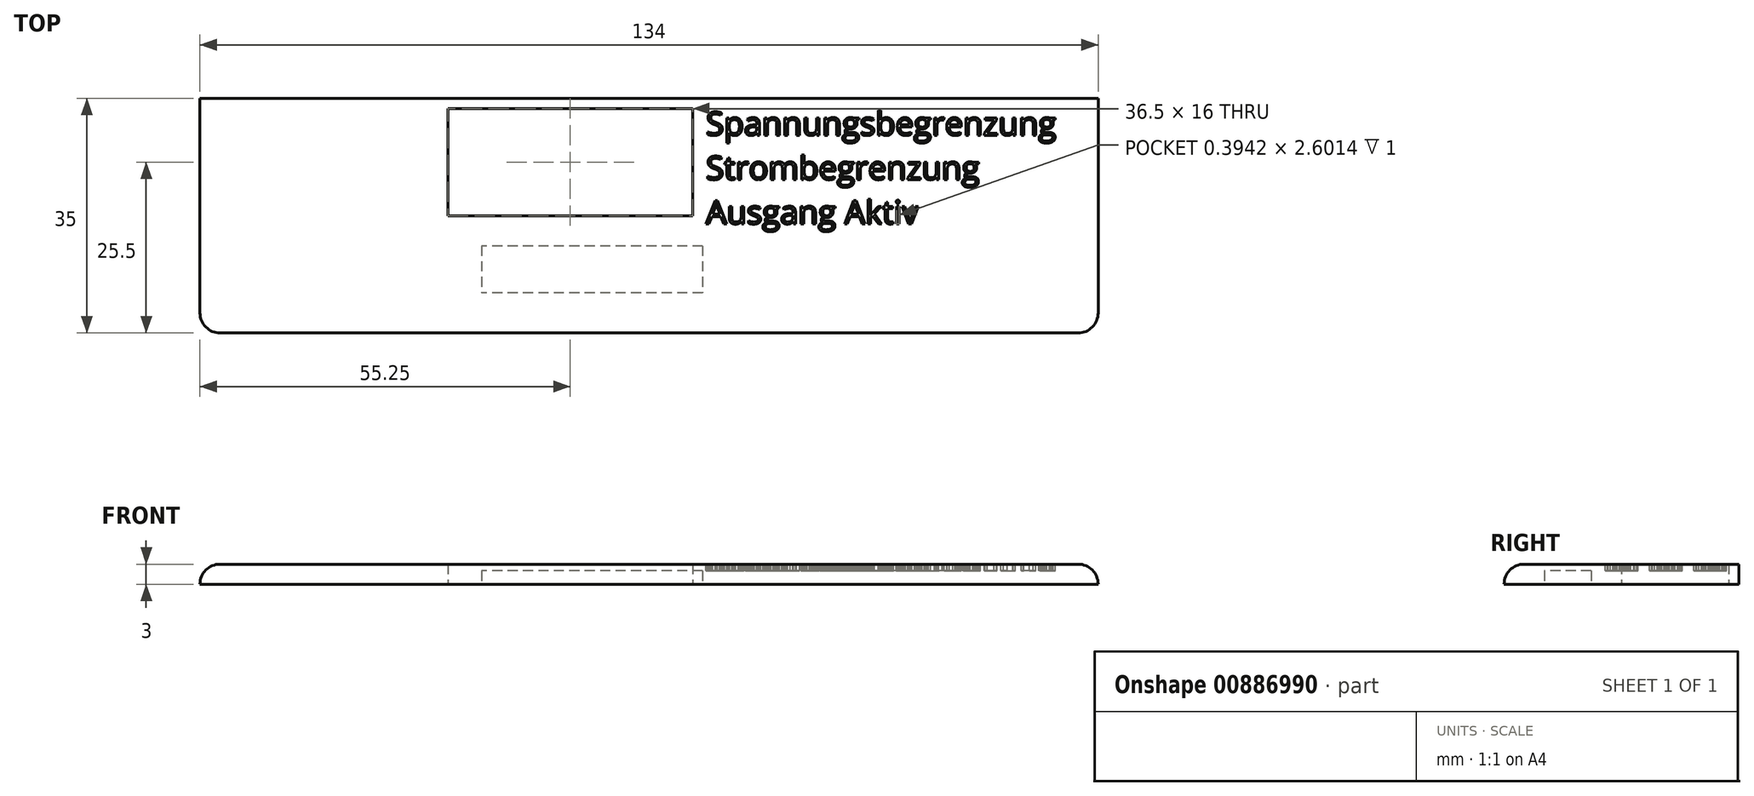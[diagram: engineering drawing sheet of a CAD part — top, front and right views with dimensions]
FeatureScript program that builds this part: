
annotation { "Feature Type Name" : "Feature", "Feature Type Description" : "" }
export const myFeature = defineFeature(function(context is Context, id is Id, definition is map)
    precondition{}
    {
        {
            var Q0;
            Q0=qCreatedBy(makeId("Top.planeOp"),FACE);
            var sketch = newSketch(context, id + "F0", { "sketchPlane" : qUnion([Q0])});
            skLineSegment(sketch, "E0.bottom", {"start": v(0, 0) * mm, "end": v(-134, 0) * mm});
            skLineSegment(sketch, "E0.top", {"start": v(0, -35) * mm, "end": v(-134, -35) * mm});
            skLineSegment(sketch, "E0.left", {"start": v(0, 0) * mm, "end": v(0, -35) * mm});
            skLineSegment(sketch, "E0.right", {"start": v(-134, 0) * mm, "end": v(-134, -35) * mm});
            skLineSegment(sketch, "E1.bottom", {"start": v(-97, -1.5) * mm, "end": v(-60.5, -1.5) * mm});
            skLineSegment(sketch, "E1.top", {"start": v(-97, -17.5) * mm, "end": v(-60.5, -17.5) * mm});
            skLineSegment(sketch, "E1.left", {"start": v(-97, -1.5) * mm, "end": v(-97, -17.5) * mm});
            skLineSegment(sketch, "E1.right", {"start": v(-60.5, -1.5) * mm, "end": v(-60.5, -17.5) * mm});
            skLineSegment(sketch, "E2.bottom", {"start": v(-59, -22) * mm, "end": v(-92, -22) * mm});
            skLineSegment(sketch, "E2.top", {"start": v(-59, -29) * mm, "end": v(-92, -29) * mm});
            skLineSegment(sketch, "E2.left", {"start": v(-59, -22) * mm, "end": v(-59, -29) * mm});
            skLineSegment(sketch, "E2.right", {"start": v(-92, -22) * mm, "end": v(-92, -29) * mm});
            skSolve(sketch);
        }
        {
            var Q0;
            Q0=makeQuery(id+"F0.imprint","IMPRINT",FACE,{"disambiguationData":[TD([[makeQuery(id+"F0.imprint","IMPRINT",EDGE,{"derivedFrom":sQuery(id+"F0.wireOp",EDGE,"E0.bottom")}),1.0]])]});
            var Q1;
            Q1=makeQuery(id+"F0.imprint","IMPRINT",FACE,{"disambiguationData":[TD([[makeQuery(id+"F0.imprint","IMPRINT",EDGE,{"derivedFrom":sQuery(id+"F0.wireOp",EDGE,"E2.bottom")}),1.0]])]});
            extrude(context, id + "F1", {"entities" : qUnion([Q0, Q1]), "depth" : 3 * mm, "offsetDistance" : 25 * mm});
        }
        {
            var Q0;
            Q0=makeQuery(id+"F1.opExtrude","CAP_EDGE",EDGE,{"disambiguationData":[OSD([sQuery(id+"F0.wireOp",EDGE,"E0.top")])],"isStart":false});
            var Q1;
            Q1=makeQuery(id+"F1.opExtrude","CAP_EDGE",EDGE,{"disambiguationData":[OSD([sQuery(id+"F0.wireOp",EDGE,"E0.right")])],"isStart":false});
            var Q2;
            Q2=makeQuery(id+"F1.opExtrude","CAP_EDGE",EDGE,{"disambiguationData":[OSD([sQuery(id+"F0.wireOp",EDGE,"E0.left")])],"isStart":false});
            var Q3;
            Q3=makeQuery(id+"F1.opExtrude","SWEPT_EDGE",EDGE,{"disambiguationData":[OSD([sQuery(id+"F0.wireOp",EDGE,"E0.top"),sQuery(id+"F0.wireOp",EDGE,"E0.right")])]});
            var Q4;
            Q4=makeQuery(id+"F1.opExtrude","SWEPT_EDGE",EDGE,{"disambiguationData":[OSD([sQuery(id+"F0.wireOp",EDGE,"E0.top"),sQuery(id+"F0.wireOp",EDGE,"E0.left")])]});
            fillet(context, id + "F2", {"entities" : qUnion([Q0, Q1, Q2, Q3, Q4]), "radius" : 3 * mm, "tangentPropagation" : true, "allowEdgeOverflow" : false});
        }
        {
            var Q0;
            Q0=makeQuery(id+"F0.imprint","IMPRINT",FACE,{"disambiguationData":[TD([[makeQuery(id+"F0.imprint","IMPRINT",EDGE,{"derivedFrom":sQuery(id+"F0.wireOp",EDGE,"E2.bottom")}),1.0]])]});
            extrude(context, id + "F3", {"entities" : qUnion([Q0]), "operationType" : NewBodyOperationType.REMOVE, "depth" : 2 * mm, "offsetDistance" : 25 * mm});
        }
        {
            var Q0;
            Q0=makeQuery(id+"F1.opExtrude","CAP_FACE",FACE,{"disambiguationData":[OSD([sQuery(id+"F0.wireOp",EDGE,"E0.bottom"),sQuery(id+"F0.wireOp",EDGE,"E0.top"),sQuery(id+"F0.wireOp",EDGE,"E0.left"),sQuery(id+"F0.wireOp",EDGE,"E0.right"),sQuery(id+"F0.wireOp",EDGE,"E1.bottom"),sQuery(id+"F0.wireOp",EDGE,"E1.top"),sQuery(id+"F0.wireOp",EDGE,"E1.left"),sQuery(id+"F0.wireOp",EDGE,"E1.right")])],"isStart":false});
            var sketch = newSketch(context, id + "F4", { "sketchPlane" : qUnion([Q0])});
            skText(sketch, "E3", { "text": "Spannungsbegrenzung\nStrombegrenzung\nAusgang Aktiv", "fontName": "OpenSans-Regular.ttf"});
            const initialGuessF4  = {"E3": [-0.0585, -0.0055, 1, 0, 0.0035]};
            skSetInitialGuess(sketch, initialGuessF4);
            skSolve(sketch);
        }
        {
            var Q0;
            Q0 = qSketchRegion(id + "F4", true);
            extrude(context, id + "F5", {"entities" : qUnion([Q0]), "operationType" : NewBodyOperationType.REMOVE, "oppositeDirection" : true, "depth" : 1 * mm, "offsetDistance" : 25 * mm});
        }
    });
